# Revit family: PRD_FrankeWS_WtrSplySystmsCtrl_ECC2FunctionController_ZA3OP0011,ZA3OP0022
name_source: partatom
category: Electrical Equipment
revit_build: Autodesk Revit 2018 (Build: 20190510_1515(x64)
units: mm (PartAtom-declared; Revit-internal decimal feet)

## family parameters
Always vertical = Yes
Cut with Voids When Loaded = No
OmniClass Number = 23.45.55.11
OmniClass Title = Sanitary Components
Part Type = Equipment Switch
Room Calculation Point = No
Round Connector Dimension = Use Diameter
Shared = No
Work Plane-Based = No

## types (2) — shared parameters
AssetType = Fixed
Category = Ss_75_70_52_96, Water supply control systems
ControllerMaterial = <By Category>
DurationUnit = year
ElectricalDeviceNominalPower = 0 W
HasProtectiveEarth = Yes
IP_Code = 20
IfcExportAs = IfcDistributionElement
IfcExportType = NOTDEFINED
InsulationStandardClass = NotKnown
Manufacturer = KWC Group AG
ManufacturerName = KWC Group AG
ManufacturerURL = www.kwc.com
NBSDescription = Water supply systems control
NBSReference = 75-75-50/110
NominalCurrent = 0 A
NominalFrequencyRange = 50
NominalVoltage = 230
NumberOfPoles = 1
PhaseAngle = 0.00°
PhaseReference = 0
ProductInformation = https://pim.kwc.com
URL = www.kwc.com
Uniclass2015Code = Ss_75_70_52_96
Uniclass2015Title = Water supply control systems
Uniclass2015Version = Systems v1.7
UsageCurrent = 0 A
Version = 1
Voltage = 230
WarrantyDurationUnit = year
zero-valued in all types: NominalHeight, NominalLength, NominalWidth

## per-type parameters (varying)
| type | BIMObjectName | Description | GrossWeight | ModelNumber | Name | NetWeight |
| ZA3OP0011 | PRD_AR_WaterSupplySystemsControl_ECC2FunctionController_ZA3OP0011 | ECC2 function controller - A3000 open with Ethernet and CAN bus connection for the fittings level and with integrated power supply, real-time clock with calendar function and WEB server. For connecting 32 AQUA 3000 open fittings/electronic system modules or up to 200 m cable length for the purpose of supplying power and external control, e.g. for adjusting fittings and for communication, 230 V AC / 24 V DC. | 1.88 kg | 2000108123 | ECC2 function controller ZA3OP0011 | 1.72 kg |
| ZA3OP0022 | PRD_AR_WaterSupplySystemsControl_ECC2FunctionController_ZA3OP0022 | ECC2 function controller - A3000 open with Ethernet and CAN bus connection for the fittings level and with integrated power supply, real-time clock with calendar function and WEB server. For connecting 32 AQUA 3000 open fittings/electronic system modules or up to 200 m cable length for the purpose of supplying power and external control, e.g. for adjusting fittings and for communication. With BMS connectivity for BacNet - IP, KNX - IP and ModBus - TCP, 230 V AC / 24 V DC. | 2.38 kg | 2030016282 | ECC2 function controller ZA3OP0022 | 2.26 kg |

note: column(s) folded — value = type name in every type: Model, ModelReference

## geometry (parser evidence)
native form markers: Sweep x2
no freeform markers — native parametric forms only
